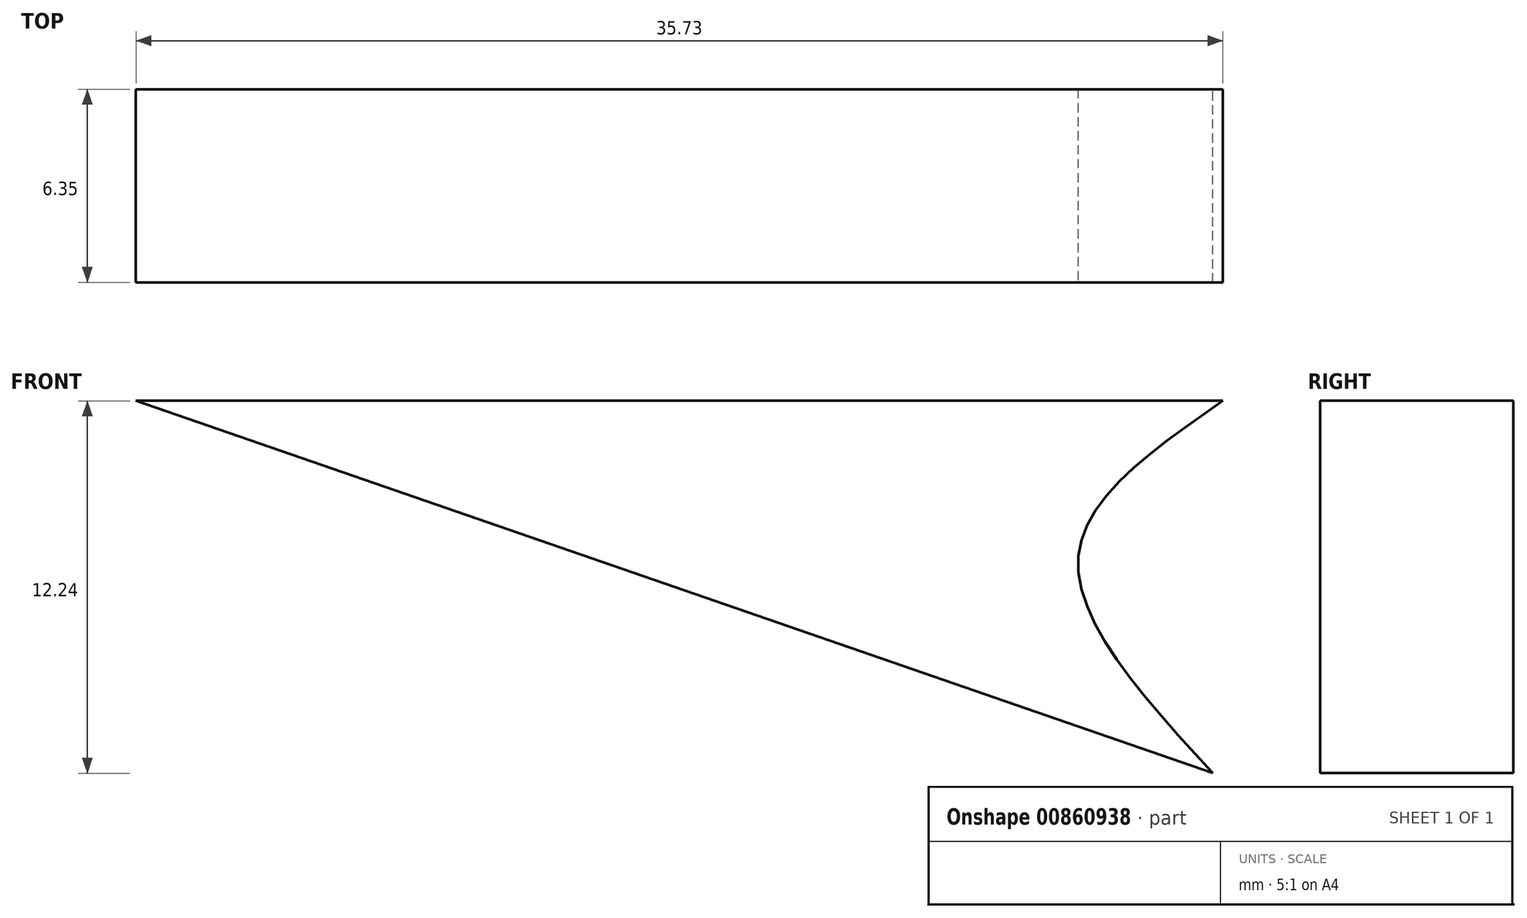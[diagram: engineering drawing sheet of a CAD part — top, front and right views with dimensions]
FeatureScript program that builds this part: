
annotation { "Feature Type Name" : "Feature", "Feature Type Description" : "" }
export const myFeature = defineFeature(function(context is Context, id is Id, definition is map)
    precondition{}
    {
        {
            var Q0;
            Q0=qCreatedBy(makeId("Front.planeOp"),FACE);
            var sketch = newSketch(context, id + "F0", { "sketchPlane" : qUnion([Q0])});
            skLineSegment(sketch, "E0", {"start": v(-42.74, 21.6) * mm, "end": v(-7, 21.6) * mm});
            skLineSegment(sketch, "E1", {"start": v(-42.74, 21.6) * mm, "end": v(-7.34, 9.35) * mm});
            skFitSpline(sketch, "E2", {"points": [v(-7, 21.6) * mm, v(-11.76, 16.52) * mm, v(-7.34, 9.35) * mm], "startDerivative": vector(-14.35, -9.95) * mm, "endDerivative": vector(13.25, -14.46) * mm});
            skSolve(sketch);
        }
        {
            var Q0;
            Q0 = qSketchRegion(id + "F0", true);
            extrude(context, id + "F1", {"entities" : qUnion([Q0]), "depth" : 6.35 * mm, "offsetDistance" : 25.4 * mm});
        }
    });
